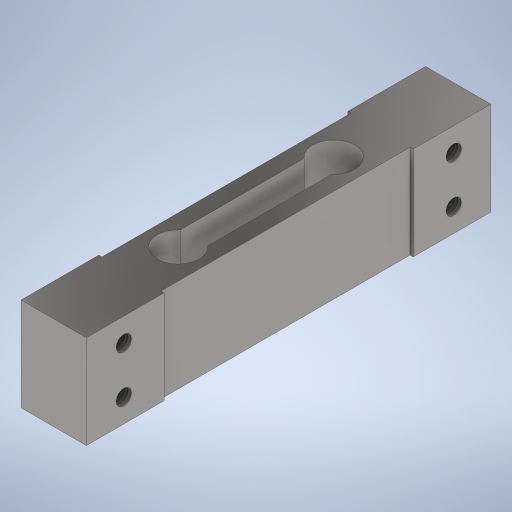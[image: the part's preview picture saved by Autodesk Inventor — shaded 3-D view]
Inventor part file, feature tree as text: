
AUTODESK INVENTOR PART (.ipt)
format: ipt  version: 2023 (Build 270158000, 158)  size: 306,688 bytes
history: native  units: mm
features: sketch x2, other x1, extrude x1, hole x1
ambient origin geometry x8: Origin, YZ Plane, XZ Plane, XY Plane, X Axis, Y Axis, Z Axis, Center Point
bodies: Body1 (feature_tree)
feature tree (5):
  other  "Sólido1"
  extrude  "Extrusão1"  Depth=130.0mm
  hole  "Furo1"  [1 undecoded]
  sketch  "Esboço1"  dims[d0=21.0mm d1=130.0mm]
  sketch  "Esboço2"  dims[d2=13.5mm d3=10.5mm d4=10.5mm d8=0.0mm d9=1.0mm d10=80.0mm d11=1.0mm d12=80.0mm d13=0.0mm d14=0.0mm d15=0.0mm d16=0.0mm d17=30.0mm d18=0.0mm d19=12.0mm d20=12.0mm d21=12.0mm d22=12.0mm d23=7.5mm d24=7.5mm d25=7.5mm d26=7.5mm d27=4.917mm d28=40.0mm d29=4.0mm d30=2.0mm d31=90.0deg d32=17.1mm d33=20.594885mm d34=8.8mm d37=0.0mm d38=4.4mm d39=50.0mm d40=25.0mm d41=25.0mm d35=1.0mm d36=1.0mm d42=20.594885mm d43=0.0625mm d44=0.75mm d45=0.375mm]
note: 1 required parameter value undecoded (feature->parameter linkage not recoverable at this tier; creation-order binding heuristic only, values carry confidence <= 0.55)
